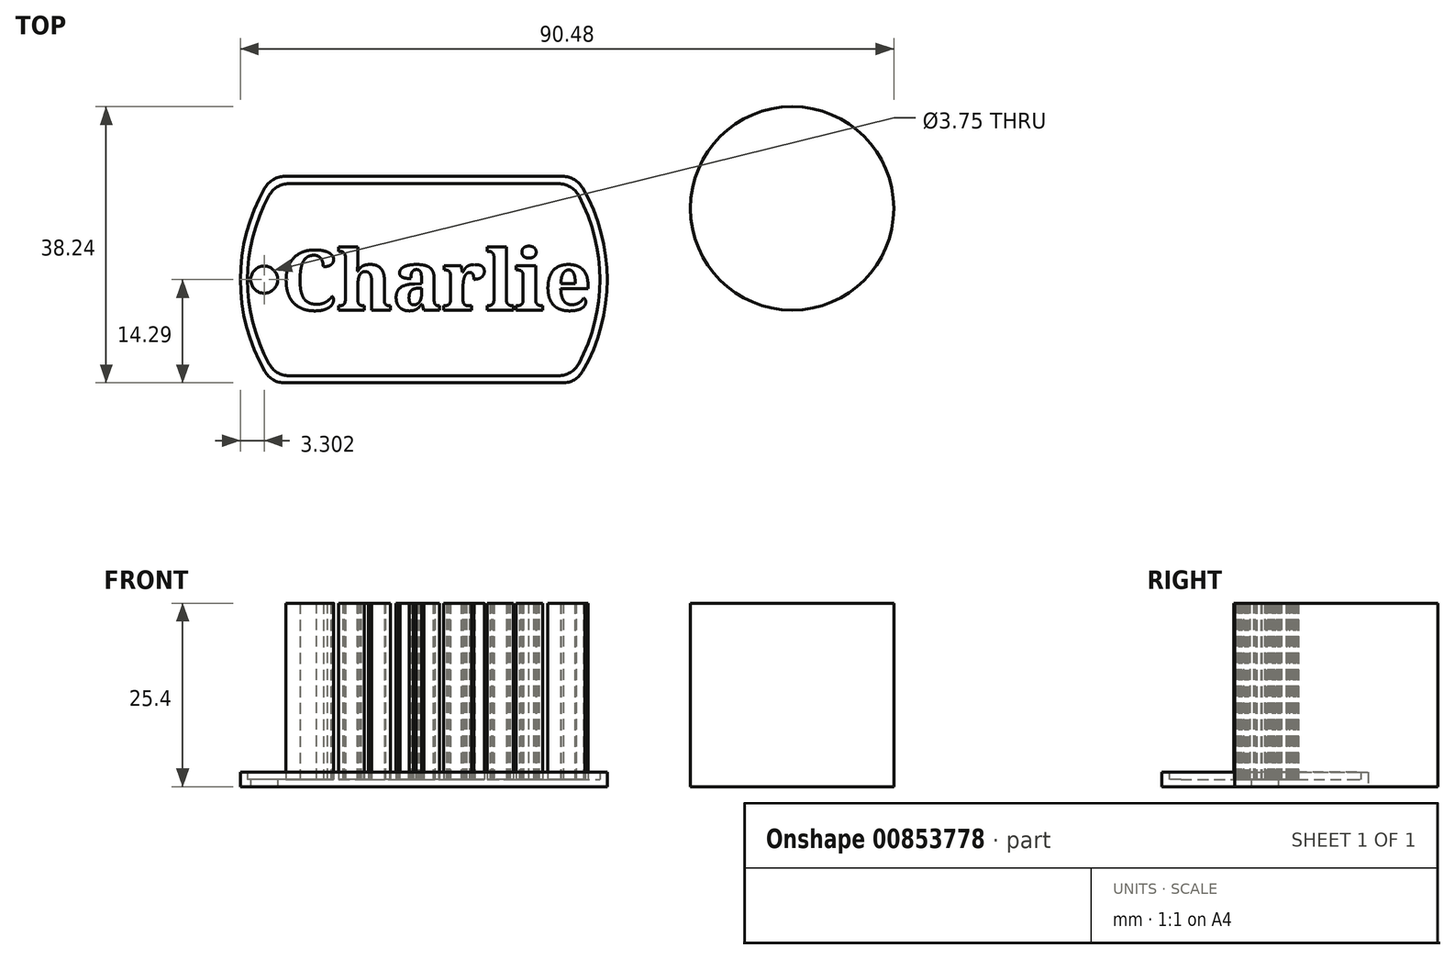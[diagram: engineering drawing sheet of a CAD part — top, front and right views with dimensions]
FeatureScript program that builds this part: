
annotation { "Feature Type Name" : "Feature", "Feature Type Description" : "" }
export const myFeature = defineFeature(function(context is Context, id is Id, definition is map)
    precondition{}
    {
        {
            var Q0;
            Q0=qCreatedBy(makeId("Top.planeOp"),FACE);
            var sketch = newSketch(context, id + "F0", { "sketchPlane" : qUnion([Q0])});
            skArc(sketch, "E0", {"start": v(-22, 12.7) * mm, "mid": v(-25.4, 0) * mm, "end": v(-22, -12.7) * mm});
            skLineSegment(sketch, "E1.top", {"start": v(-19.25, -14.29) * mm, "end": v(19.25, -14.29) * mm});
            skArc(sketch, "E2.trimOffspring", {"start": v(22, -12.7) * mm, "mid": v(25.4, 0) * mm, "end": v(22, 12.7) * mm});
            skLineSegment(sketch, "E3", {"start": v(-19.25, 14.29) * mm, "end": v(19.25, 14.29) * mm});
            skPoint(sketch, "E4.visualSharp", {"position": v(-21, 14.29) * mm});
            skArc(sketch, "E4.filletArc", {"start": v(-19.25, 14.29) * mm, "mid": v(-20.83, 13.86) * mm, "end": v(-22, 12.7) * mm});
            skPoint(sketch, "E5.visualSharp", {"position": v(21, 14.29) * mm});
            skArc(sketch, "E5.filletArc", {"start": v(22, 12.7) * mm, "mid": v(20.83, 13.86) * mm, "end": v(19.25, 14.29) * mm});
            skPoint(sketch, "E6.visualSharp", {"position": v(21, -14.29) * mm});
            skArc(sketch, "E6.filletArc", {"start": v(19.25, -14.29) * mm, "mid": v(20.83, -13.86) * mm, "end": v(22, -12.7) * mm});
            skPoint(sketch, "E7.visualSharp", {"position": v(-21, -14.29) * mm});
            skArc(sketch, "E7.filletArc", {"start": v(-22, -12.7) * mm, "mid": v(-20.83, -13.86) * mm, "end": v(-19.25, -14.29) * mm});
            skCircle(sketch, "E8", {"center": v(-22.1, 0) * mm, "radius": 1.87 * mm});
            skSolve(sketch);
        }
        {
            var Q0;
            Q0=makeQuery(id+"F0.imprint","IMPRINT",FACE,{"disambiguationData":[TD([[makeQuery(id+"F0.imprint","IMPRINT",EDGE,{"derivedFrom":sQuery(id+"F0.wireOp",EDGE,"E0")}),1.0]])]});
            extrude(context, id + "F1", {"entities" : qUnion([Q0]), "depth" : 1 * mm, "offsetDistance" : 25.4 * mm});
        }
        {
            var Q0;
            Q0=makeQuery(id+"F1.opExtrude","CAP_FACE",FACE,{"disambiguationData":[OSD([sQuery(id+"F0.wireOp",EDGE,"E0"),sQuery(id+"F0.wireOp",EDGE,"E1.top"),sQuery(id+"F0.wireOp",EDGE,"E2.trimOffspring"),sQuery(id+"F0.wireOp",EDGE,"E3"),sQuery(id+"F0.wireOp",EDGE,"E4.filletArc"),sQuery(id+"F0.wireOp",EDGE,"E5.filletArc"),sQuery(id+"F0.wireOp",EDGE,"E6.filletArc"),sQuery(id+"F0.wireOp",EDGE,"E7.filletArc")])],"isStart":false});
            var sketch = newSketch(context, id + "F2", { "sketchPlane" : qUnion([Q0])});
            skLineSegment(sketch, "E9.0", {"start": v(-18.66, 13.29) * mm, "end": v(18.66, 13.29) * mm});
            skArc(sketch, "E9.1", {"start": v(-21.45, 11.63) * mm, "mid": v(-24.4, 0) * mm, "end": v(-21.45, -11.63) * mm});
            skLineSegment(sketch, "E9.2", {"start": v(-18.66, -13.29) * mm, "end": v(18.66, -13.29) * mm});
            skArc(sketch, "E9.3", {"start": v(21.45, -11.63) * mm, "mid": v(24.4, 0) * mm, "end": v(21.45, 11.63) * mm});
            skPoint(sketch, "E10.visualSharp", {"position": v(-20.46, 13.29) * mm});
            skArc(sketch, "E10.filletArc", {"start": v(-18.66, 13.29) * mm, "mid": v(-20.29, 12.84) * mm, "end": v(-21.45, 11.63) * mm});
            skPoint(sketch, "E11.visualSharp", {"position": v(20.46, 13.29) * mm});
            skArc(sketch, "E11.filletArc", {"start": v(21.45, 11.63) * mm, "mid": v(20.29, 12.84) * mm, "end": v(18.66, 13.29) * mm});
            skPoint(sketch, "E12.visualSharp", {"position": v(20.46, -13.29) * mm});
            skArc(sketch, "E12.filletArc", {"start": v(18.66, -13.29) * mm, "mid": v(20.29, -12.84) * mm, "end": v(21.45, -11.63) * mm});
            skPoint(sketch, "E13.visualSharp", {"position": v(-20.46, -13.29) * mm});
            skArc(sketch, "E13.filletArc", {"start": v(-21.45, -11.63) * mm, "mid": v(-20.29, -12.84) * mm, "end": v(-18.66, -13.29) * mm});
            skLineSegment(sketch, "E14.0", {"start": v(-19.25, 14.29) * mm, "end": v(19.25, 14.29) * mm});
            skArc(sketch, "E14.1", {"start": v(-22, 12.7) * mm, "mid": v(-25.4, 0) * mm, "end": v(-22, -12.7) * mm});
            skLineSegment(sketch, "E14.2", {"start": v(-19.25, -14.29) * mm, "end": v(19.25, -14.29) * mm});
            skArc(sketch, "E14.3", {"start": v(22, -12.7) * mm, "mid": v(25.4, 0) * mm, "end": v(22, 12.7) * mm});
            skPoint(sketch, "E15.visualSharp", {"position": v(-21, -14.29) * mm});
            skArc(sketch, "E15.filletArc", {"start": v(-22, -12.7) * mm, "mid": v(-20.83, -13.86) * mm, "end": v(-19.25, -14.29) * mm});
            skPoint(sketch, "E16.visualSharp", {"position": v(21, -14.29) * mm});
            skArc(sketch, "E16.filletArc", {"start": v(19.25, -14.29) * mm, "mid": v(20.83, -13.86) * mm, "end": v(22, -12.7) * mm});
            skPoint(sketch, "E17.visualSharp", {"position": v(21, 14.29) * mm});
            skArc(sketch, "E17.filletArc", {"start": v(22, 12.7) * mm, "mid": v(20.83, 13.86) * mm, "end": v(19.25, 14.29) * mm});
            skPoint(sketch, "E18.visualSharp", {"position": v(-21, 14.29) * mm});
            skArc(sketch, "E18.filletArc", {"start": v(-19.25, 14.29) * mm, "mid": v(-20.83, 13.86) * mm, "end": v(-22, 12.7) * mm});
            skSolve(sketch);
        }
        {
            var Q0;
            Q0=makeQuery(id+"F2.imprint","IMPRINT",FACE,{"disambiguationData":[TD([[makeQuery(id+"F2.imprint","IMPRINT",EDGE,{"derivedFrom":sQuery(id+"F2.wireOp",EDGE,"E9.0")}),1.0]])]});
            extrude(context, id + "F3", {"entities" : qUnion([Q0]), "operationType" : NewBodyOperationType.ADD, "depth" : 1 * mm, "offsetDistance" : 25.4 * mm});
        }
        {
            var Q0;
            Q0=qCreatedBy(makeId("Top.planeOp"),FACE);
            var sketch = newSketch(context, id + "F4", { "sketchPlane" : qUnion([Q0])});
            skText(sketch, "E19", { "text": "Charlie", "fontName": "NotoSerif-Bold.ttf"});
            skCircle(sketch, "E20", {"center": v(51, 9.87) * mm, "radius": 14.08 * mm});
            const initialGuessF4  = {"E19": [-0.0197, -0.00421, 1, 0, 0.00828]};
            skSetInitialGuess(sketch, initialGuessF4);
            skSolve(sketch);
        }
        {
            var Q0;
            Q0=makeQuery(id+"F4.imprint","IMPRINT",FACE,{"disambiguationData":[TD([[makeQuery(id+"F4.imprint","IMPRINT",EDGE,{"derivedFrom":sQuery(id+"F4.wireOp",EDGE,"E19.sketch_text.stroke-0")}),-1.0]])]});
            var Q1;
            Q1=makeQuery(id+"F4.imprint","IMPRINT",FACE,{"disambiguationData":[TD([[makeQuery(id+"F4.imprint","IMPRINT",EDGE,{"derivedFrom":sQuery(id+"F4.wireOp",EDGE,"E19.sketch_text.stroke-38")}),-1.0]])]});
            var Q2;
            Q2=makeQuery(id+"F4.imprint","IMPRINT",FACE,{"disambiguationData":[TD([[makeQuery(id+"F4.imprint","IMPRINT",EDGE,{"derivedFrom":sQuery(id+"F4.wireOp",EDGE,"E19.sketch_text.stroke-142")}),-1.0]])]});
            var Q3;
            Q3=makeQuery(id+"F4.imprint","IMPRINT",FACE,{"disambiguationData":[TD([[makeQuery(id+"F4.imprint","IMPRINT",EDGE,{"derivedFrom":sQuery(id+"F4.wireOp",EDGE,"E19.sketch_text.stroke-184")}),-1.0]])]});
            var Q4;
            Q4=makeQuery(id+"F4.imprint","IMPRINT",FACE,{"disambiguationData":[TD([[makeQuery(id+"F4.imprint","IMPRINT",EDGE,{"derivedFrom":sQuery(id+"F4.wireOp",EDGE,"E19.sketch_text.stroke-206")}),-1.0]])]});
            var Q5;
            Q5=makeQuery(id+"F4.imprint","IMPRINT",FACE,{"disambiguationData":[TD([[makeQuery(id+"F4.imprint","IMPRINT",EDGE,{"derivedFrom":sQuery(id+"F4.wireOp",EDGE,"E19.sketch_text.stroke-222")}),-1.0]])]});
            var Q6;
            Q6=makeQuery(id+"F4.imprint","IMPRINT",FACE,{"disambiguationData":[TD([[makeQuery(id+"F4.imprint","IMPRINT",EDGE,{"derivedFrom":sQuery(id+"F4.wireOp",EDGE,"E19.sketch_text.stroke-90")}),-1.0]])]});
            var Q7;
            Q7=makeQuery(id+"F4.imprint","IMPRINT",FACE,{"disambiguationData":[TD([[makeQuery(id+"F4.imprint","IMPRINT",EDGE,{"derivedFrom":sQuery(id+"F4.wireOp",EDGE,"E19.sketch_text.stroke-244")}),-1.0]])]});
            var Q8;
            Q8=makeQuery(id+"F4.imprint","IMPRINT",FACE,{"disambiguationData":[TD([[makeQuery(id+"F4.imprint","IMPRINT",EDGE,{"derivedFrom":sQuery(id+"F4.wireOp",EDGE,"E20")}),1.0]])]});
            extrude(context, id + "F5", {"entities" : qUnion([Q0, Q1, Q2, Q3, Q4, Q5, Q6, Q7, Q8]), "operationType" : NewBodyOperationType.ADD, "depth" : 25.4 * mm, "offsetDistance" : 25.4 * mm});
        }
    });
